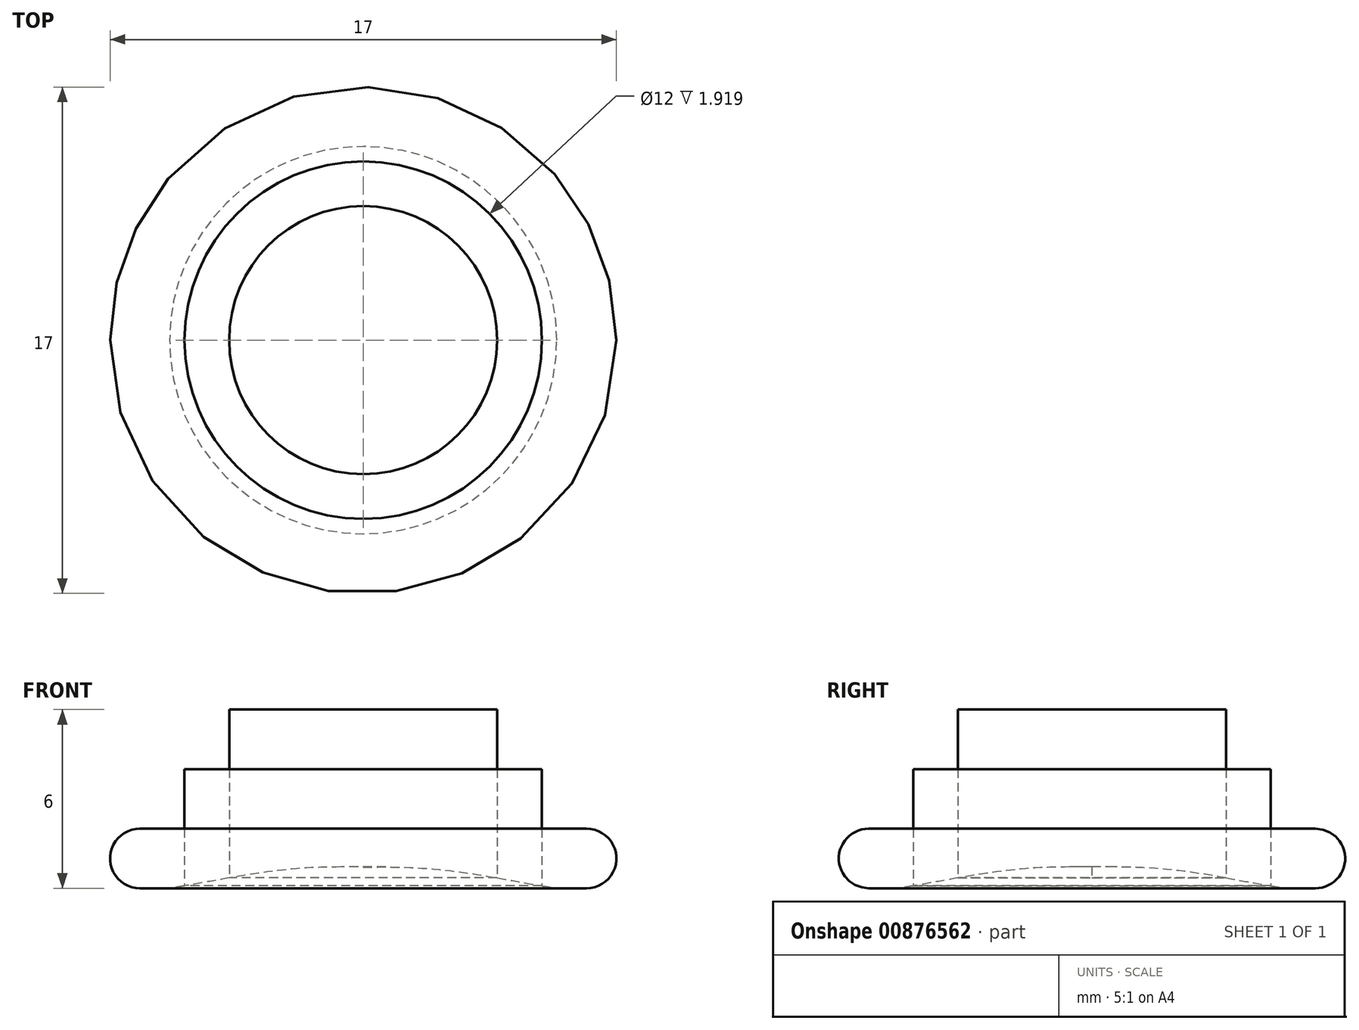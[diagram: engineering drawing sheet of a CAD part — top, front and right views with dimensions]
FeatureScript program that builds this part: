
annotation { "Feature Type Name" : "Feature", "Feature Type Description" : "" }
export const myFeature = defineFeature(function(context is Context, id is Id, definition is map)
    precondition{}
    {
        {
            var Q0;
            Q0=qCreatedBy(makeId("Top.planeOp"),FACE);
            var sketch = newSketch(context, id + "F0", { "sketchPlane" : qUnion([Q0])});
            skCircle(sketch, "E0", {"center": v(0, 0) * mm, "radius": 4.5 * mm});
            skCircle(sketch, "E1", {"center": v(0, 0) * mm, "radius": 6 * mm});
            skCircle(sketch, "E2", {"center": v(0, 0) * mm, "radius": 8.5 * mm});
            skSolve(sketch);
        }
        {
            var Q0;
            Q0=makeQuery(id+"F0.imprint","IMPRINT",FACE,{"disambiguationData":[TD([[makeQuery(id+"F0.imprint","IMPRINT",EDGE,{"derivedFrom":sQuery(id+"F0.wireOp",EDGE,"E0")}),1.0]])]});
            extrude(context, id + "F1", {"entities" : qUnion([Q0]), "depth" : 6 * mm, "offsetDistance" : 25 * mm});
        }
        {
            var Q0;
            Q0=makeQuery(id+"F0.imprint","IMPRINT",FACE,{"disambiguationData":[TD([[makeQuery(id+"F0.imprint","IMPRINT",EDGE,{"derivedFrom":sQuery(id+"F0.wireOp",EDGE,"E0")}),-1.0]])]});
            extrude(context, id + "F2", {"entities" : qUnion([Q0]), "depth" : 4 * mm, "offsetDistance" : 25 * mm});
        }
        {
            var Q0;
            Q0=makeQuery(id+"F0.imprint","IMPRINT",FACE,{"disambiguationData":[TD([[makeQuery(id+"F0.imprint","IMPRINT",EDGE,{"derivedFrom":sQuery(id+"F0.wireOp",EDGE,"E1")}),-1.0]])]});
            extrude(context, id + "F3", {"entities" : qUnion([Q0]), "depth" : 2 * mm, "offsetDistance" : 25 * mm});
        }
        {
            var Q0;
            Q0=makeQuery(id+"F3.opExtrude","CAP_EDGE",EDGE,{"disambiguationData":[OSD([sQuery(id+"F0.wireOp",EDGE,"E2")])],"isStart":true});
            var Q1;
            Q1=makeQuery(id+"F3.opExtrude","CAP_EDGE",EDGE,{"disambiguationData":[OSD([sQuery(id+"F0.wireOp",EDGE,"E2")])],"isStart":false});
            fillet(context, id + "F4", {"entities" : qUnion([Q0, Q1]), "radius" : 1 * mm, "tangentPropagation" : true, "allowEdgeOverflow" : false});
        }
        {
            var Q0;
            Q0=qCreatedBy(makeId("Front.planeOp"),FACE);
            var sketch = newSketch(context, id + "F5", { "sketchPlane" : qUnion([Q0])});
            skLineSegment(sketch, "E3", {"start": v(0, 0) * mm, "end": v(6.5, 0) * mm});
            skLineSegment(sketch, "E4", {"start": v(0, 0) * mm, "end": v(0, 0.7) * mm});
            skFitSpline(sketch, "E5", {"points": [v(0, 0.7) * mm, v(6.5, 0) * mm], "startDerivative": vector(8.33, 0.29) * mm, "endDerivative": vector(6.93, -1.08) * mm});
            skSolve(sketch);
        }
        {
            var Q0;
            Q0=makeQuery(id+"F5.imprint","IMPRINT",FACE,{"disambiguationData":[TD([[makeQuery(id+"F5.imprint","IMPRINT",EDGE,{"derivedFrom":sQuery(id+"F5.wireOp",EDGE,"E3")}),1.0]])]});
            var Q1;
            Q1=sQuery(id+"F5.wireOp",EDGE,"E4");
            revolve(context, id + "F6", {"operationType" : NewBodyOperationType.REMOVE, "surfaceOperationType" : NewSurfaceOperationType.NEW, "entities" : qUnion([Q0]), "axis" : qUnion([Q1]), "revolveType" : RevolveType.FULL, "oppositeDirection" : true});
        }
    });
